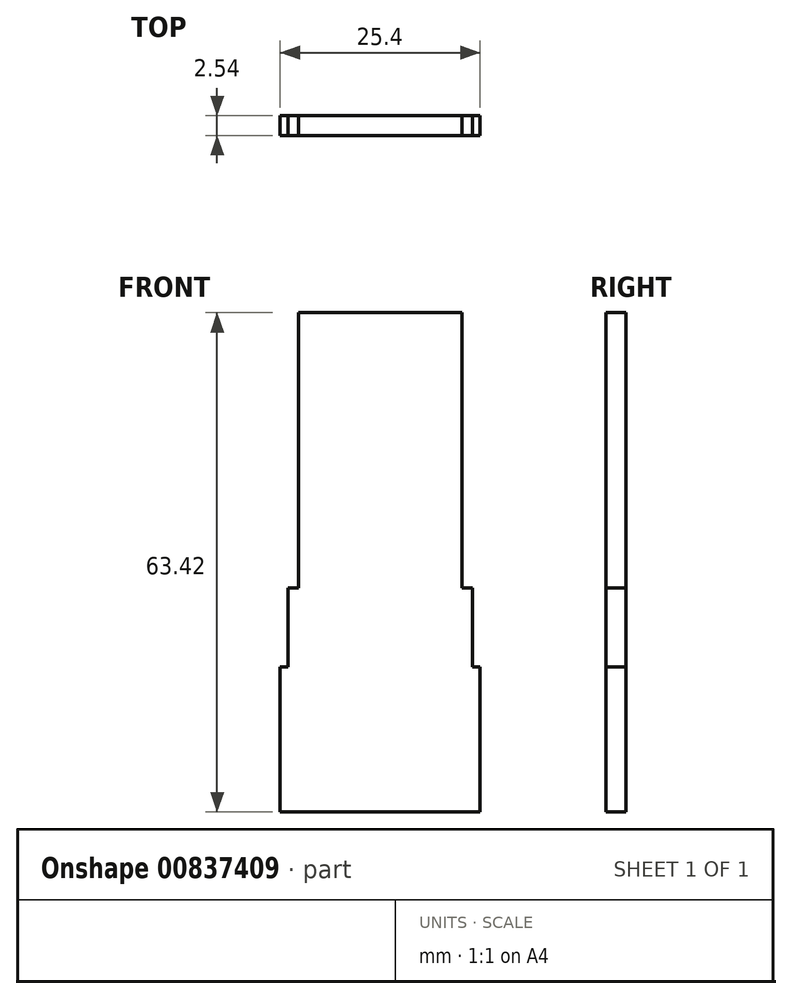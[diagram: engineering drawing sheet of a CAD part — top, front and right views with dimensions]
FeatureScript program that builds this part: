
annotation { "Feature Type Name" : "Feature", "Feature Type Description" : "" }
export const myFeature = defineFeature(function(context is Context, id is Id, definition is map)
    precondition{}
    {
        {
            var Q0;
            Q0=qCreatedBy(makeId("Front.planeOp"),FACE);
            var sketch = newSketch(context, id + "F0", { "sketchPlane" : qUnion([Q0])});
            skLineSegment(sketch, "E0", {"start": v(0, 0) * mm, "end": v(-12.7, 0) * mm});
            skLineSegment(sketch, "E1.MirrorCS", {"start": v(0, 0) * mm, "end": v(12.7, 0) * mm});
            skLineSegment(sketch, "E2", {"start": v(-12.7, 0) * mm, "end": v(-12.7, 9.5) * mm});
            skLineSegment(sketch, "E3", {"start": v(-12.7, 9.5) * mm, "end": v(12.7, 9.5) * mm});
            skLineSegment(sketch, "E4", {"start": v(12.7, 9.5) * mm, "end": v(12.7, 0) * mm});
            skLineSegment(sketch, "E5", {"start": v(-12.7, 9.5) * mm, "end": v(-12.7, 18.44) * mm});
            skLineSegment(sketch, "E6", {"start": v(-12.7, 18.44) * mm, "end": v(12.7, 18.44) * mm});
            skLineSegment(sketch, "E7", {"start": v(12.7, 18.44) * mm, "end": v(12.7, 9.5) * mm});
            skLineSegment(sketch, "E8", {"start": v(-11.73, 18.44) * mm, "end": v(-11.73, 28.45) * mm});
            skLineSegment(sketch, "E9", {"start": v(11.73, 18.44) * mm, "end": v(11.73, 28.45) * mm});
            skLineSegment(sketch, "E10", {"start": v(11.73, 28.45) * mm, "end": v(-11.73, 28.45) * mm});
            skLineSegment(sketch, "E11", {"start": v(-10.38, 28.45) * mm, "end": v(-10.38, 63.42) * mm});
            skLineSegment(sketch, "E12", {"start": v(10.38, 28.45) * mm, "end": v(10.38, 63.42) * mm});
            skLineSegment(sketch, "E13", {"start": v(10.38, 63.42) * mm, "end": v(-10.38, 63.42) * mm});
            skSolve(sketch);
        }
        {
            var Q0;
            Q0=makeQuery(id+"F0.imprint","IMPRINT",FACE,{"disambiguationData":[TD([[makeQuery(id+"F0.imprint","IMPRINT",EDGE,{"derivedFrom":sQuery(id+"F0.wireOp",EDGE,"E0")}),-1.0]])]});
            var Q1;
            Q1=makeQuery(id+"F0.imprint","IMPRINT",FACE,{"disambiguationData":[TD([[makeQuery(id+"F0.imprint","IMPRINT",EDGE,{"derivedFrom":sQuery(id+"F0.wireOp",EDGE,"E3")}),1.0]])]});
            var Q2;
            {var subQ1=sQuery(id+"F0.wireOp",EDGE,"E8");Q2=makeQuery(id+"F0.imprint","IMPRINT",FACE,{"disambiguationData":[TD([[makeQuery(id+"F0.imprint","IMPRINT",EDGE,{"derivedFrom":subQ1}),-1.0]])]});}
            var Q3;
            {var subQ0=sQuery(id+"F0.wireOp",EDGE,"E11");Q3=makeQuery(id+"F0.imprint","IMPRINT",FACE,{"disambiguationData":[TD([[makeQuery(id+"F0.imprint","IMPRINT",EDGE,{"derivedFrom":subQ0}),-1.0]])]});}
            extrude(context, id + "F1", {"entities" : qUnion([Q0, Q1, Q2, Q3]), "oppositeDirection" : true, "depth" : 2.54 * mm, "offsetDistance" : 25.4 * mm});
        }
    });
